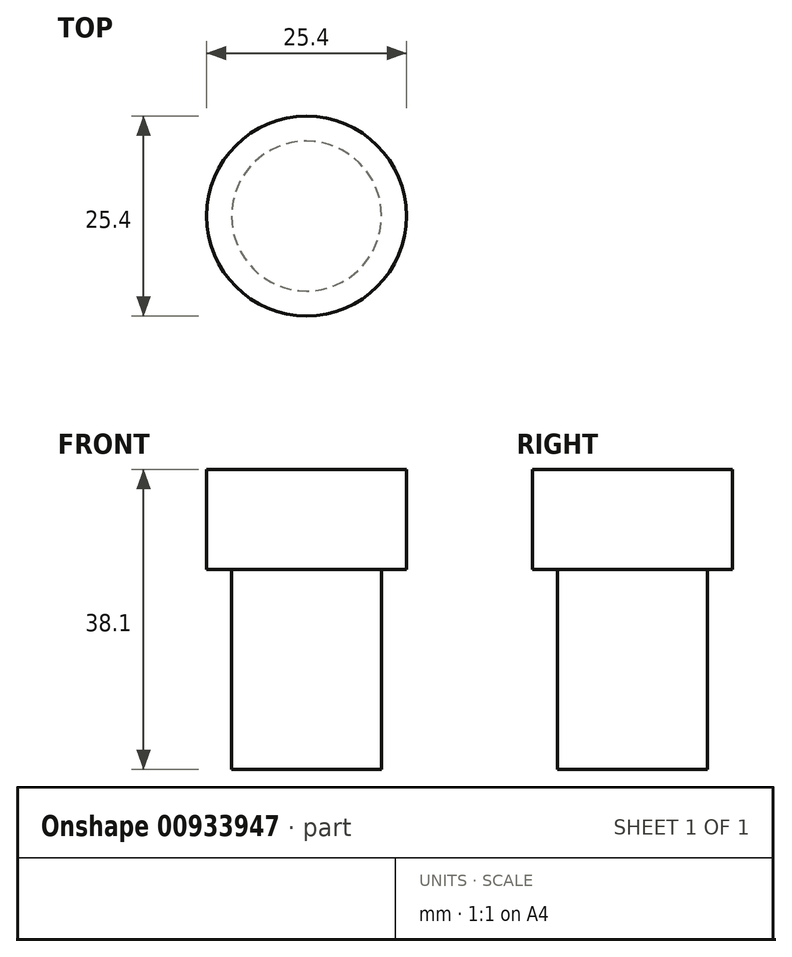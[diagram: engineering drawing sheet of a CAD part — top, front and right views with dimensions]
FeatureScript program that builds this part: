
annotation { "Feature Type Name" : "Feature", "Feature Type Description" : "" }
export const myFeature = defineFeature(function(context is Context, id is Id, definition is map)
    precondition{}
    {
        {
            var Q0;
            Q0=qCreatedBy(makeId("Front.planeOp"),FACE);
            var sketch = newSketch(context, id + "F0", { "sketchPlane" : qUnion([Q0])});
            skLineSegment(sketch, "E0", {"start": v(0, 0) * mm, "end": v(0, 12.7) * mm});
            skLineSegment(sketch, "E1", {"start": v(0, 12.7) * mm, "end": v(12.7, 12.7) * mm});
            skLineSegment(sketch, "E2", {"start": v(12.7, 12.7) * mm, "end": v(12.7, 0) * mm});
            skLineSegment(sketch, "E3", {"start": v(12.7, 0) * mm, "end": v(9.52, 0) * mm});
            skLineSegment(sketch, "E4", {"start": v(9.52, 0) * mm, "end": v(9.52, -25.4) * mm});
            skLineSegment(sketch, "E5", {"start": v(9.53, -25.4) * mm, "end": v(0, -25.4) * mm});
            skLineSegment(sketch, "E6", {"start": v(0, -25.4) * mm, "end": v(0, 0) * mm});
            skLineSegment(sketch, "E7", {"start": v(0, -41.4) * mm, "end": v(0, -41.4) * mm});
            skLineSegment(sketch, "E8", {"start": v(0, -50.8) * mm, "end": v(0, 50.8) * mm, "construction": true});
            skSolve(sketch);
        }
        {
            var Q0;
            Q0=makeQuery(id+"F0.imprint","IMPRINT",FACE,{"disambiguationData":[TD([[makeQuery(id+"F0.imprint","IMPRINT",EDGE,{"derivedFrom":sQuery(id+"F0.wireOp",EDGE,"E0")}),-1.0]])]});
            var Q1;
            Q1=sQuery(id+"F0.wireOp",EDGE,"E8");
            revolve(context, id + "F1", {"surfaceOperationType" : NewSurfaceOperationType.NEW, "entities" : qUnion([Q0]), "axis" : qUnion([Q1]), "revolveType" : RevolveType.FULL});
        }
    });
